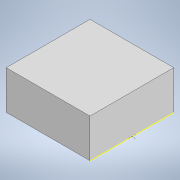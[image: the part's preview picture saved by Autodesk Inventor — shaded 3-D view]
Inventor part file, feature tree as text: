
AUTODESK INVENTOR PART (.ipt)
format: ipt  version: 2022 (Build 260153000, 153)  size: 109,056 bytes
history: native  units: in
note: dims shown in document units (in); Inventor stores cm internally (conversion verified against a paired STEP export)
features: sketch x3, extrude x2
ambient origin geometry x8: Origin, YZ Plane, XZ Plane, XY Plane, X Axis, Y Axis, Z Axis, Center Point
bodies: Solid1 (feature_tree)
feature tree (5):
  extrude  "Extrusion1"  Depth=0.2165in
  extrude  "Extrusion2"  Depth=0.2559in
  sketch  "Sketch5"  dims[d8=0.0787in d9=0.0in d10=0.2559in d11=0.0394in d12=0.0in]
  sketch  "Sketch2"  dims[d2=0.2165in d3=0.2165in]
  sketch  "Sketch4"  dims[d6=0.2559in d7=0.2559in]
